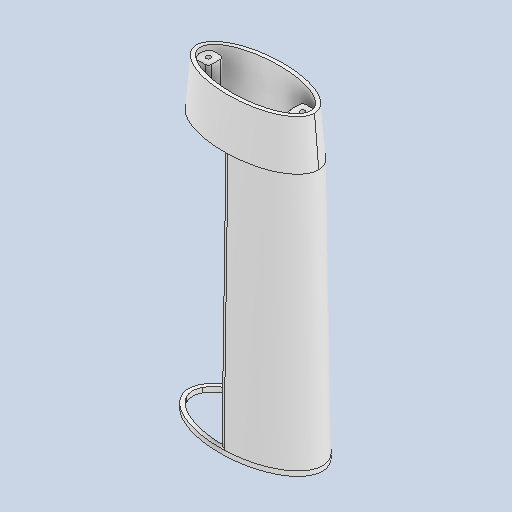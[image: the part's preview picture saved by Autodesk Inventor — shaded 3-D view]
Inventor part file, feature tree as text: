
AUTODESK INVENTOR PART (.ipt)
format: ipt  version: 2022 (Build 260153000, 153)  size: 320,000 bytes
history: native  units: in
note: dims shown in document units (in); Inventor stores cm internally (conversion verified against a paired STEP export)
features: sketch x10, plane x4, extrude x4, loft x2, fillet x2, hole x2
ambient origin geometry x8: Origin, YZ Plane, XZ Plane, XY Plane, X Axis, Y Axis, Z Axis, Center Point
bodies: Body1 (feature_tree)
feature tree (24):
  plane  "Work Plane4"
  sketch  "Sketch25"  dims[d137=6.3583in d169=0.0in d170=90.0deg]
  sketch  "Sketch26"  dims[d171=0.0in d172=90.0deg d177=0.0in]
  loft  "Loft4"
  plane  "Work Plane9"
  loft  "Loft5"
  extrude  "Extrusion11"  TaperAngle=0.0deg  [1 undecoded]
  fillet  "Fillet3"  [1 undecoded]
  extrude  "Extrusion12"  Depth=0.0787in
  hole  "Hole6"  [1 undecoded]
  extrude  "Extrusion13"  Depth=0.1181in TaperAngle=0.0deg
  fillet  "Fillet4"  Radius=0.0787in
  hole  "Hole7"  [1 undecoded]
  extrude  "Extrusion14"  Depth=0.0394in
  plane  "Work Plane7"
  plane  "Work Plane8"
  sketch  "Sketch29"  dims[d178=0.7874in d179=0.3937in d186=0.0in d187=90.0deg d188=0.0in d189=90.0deg]
  sketch  "Sketch31"  dims[d197=1.1811in d198=0.0in d199=0.0787in]
  sketch  "Sketch32"  dims[d200=1.378in d201=0.1181in d202=0.0in]
  sketch  "Sketch34"  dims[d205=0.1181in d206=0.2362in d207=0.1575in d208=0.0787in d209=90.0deg d210=0.1181in d211=0.0in d217=0.1181in d218=0.0in d219=0.0787in]
  sketch  "Sketch35"  dims[d220=1.378in]
  sketch  "Sketch36"  dims[d221=0.1181in d222=0.2362in d223=0.1575in d224=0.0787in d225=90.0deg d226=0.2362in d227=0.0in d228=0.1181in d229=0.0in]
  sketch  "Sketch37"  dims[d230=0.0394in d231=0.0394in]
  sketch  "Sketch38"  dims[d232=0.0394in d233=0.0059in d234=0.0098in d235=0.0148in d236=0.5635in d237=0.0295in d238=0.8108in d239=0.0025in d240=0.0295in d241=0.0148in]
note: 4 required parameter values undecoded (feature->parameter linkage not recoverable at this tier; creation-order binding heuristic only, values carry confidence <= 0.55)
